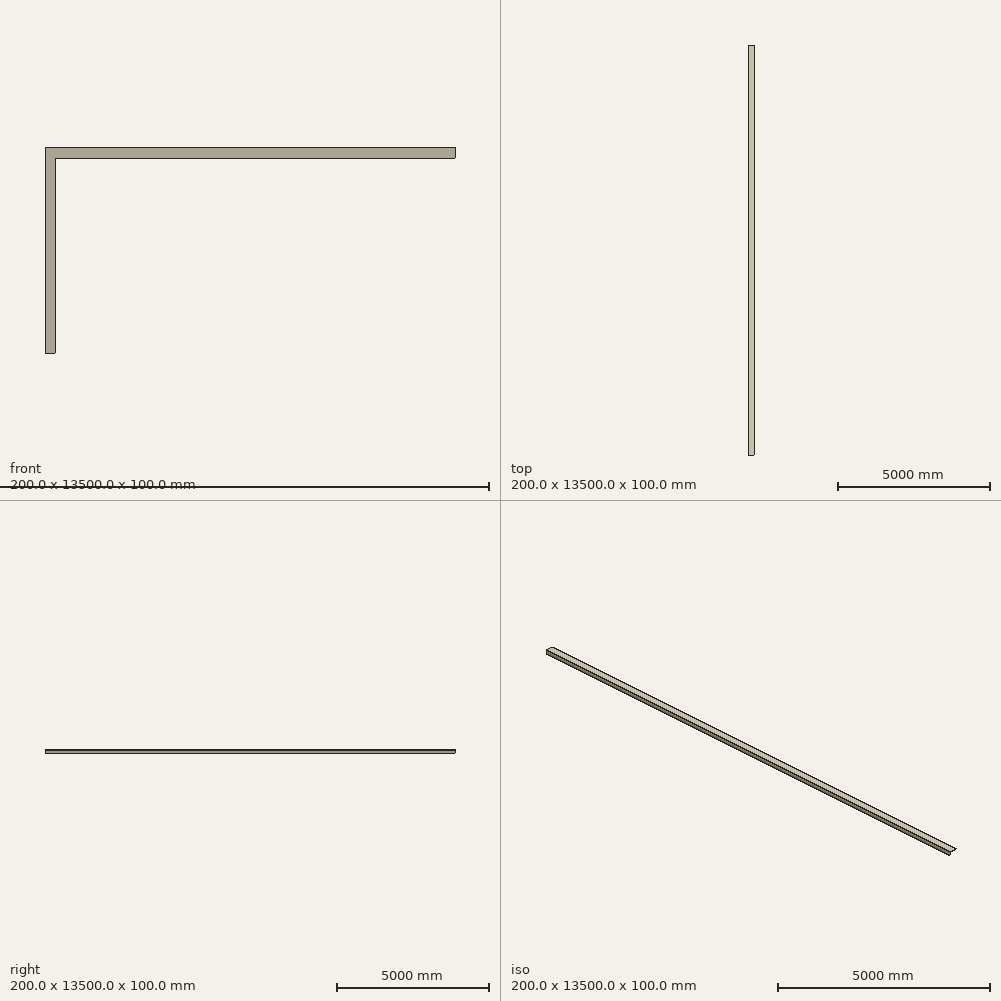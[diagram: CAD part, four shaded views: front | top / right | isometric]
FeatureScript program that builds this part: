
annotation { "Feature Type Name" : "Feature", "Feature Type Description" : "" }
export const myFeature = defineFeature(function(context is Context, id is Id, definition is map)
    precondition{}
    {
        {
            var Q0;
            Q0=qCreatedBy(makeId("Front.planeOp"),FACE);
            var sketch = newSketch(context, id + "F0", { "sketchPlane" : qUnion([Q0])});
            skLineSegment(sketch, "E0", {"start": v(0, 0) * mm, "end": v(0, 100) * mm});
            skLineSegment(sketch, "E1", {"start": v(0, 100) * mm, "end": v(200, 100) * mm});
            skLineSegment(sketch, "E2", {"start": v(200, 100) * mm, "end": v(200, 95) * mm});
            skLineSegment(sketch, "E3", {"start": v(200, 95) * mm, "end": v(5, 95) * mm});
            skLineSegment(sketch, "E4", {"start": v(5, 95) * mm, "end": v(5, 0) * mm});
            skLineSegment(sketch, "E5", {"start": v(5, 0) * mm, "end": v(0, 0) * mm});
            skSolve(sketch);
        }
        {
            var Q0;
            Q0 = qSketchRegion(id + "F0", true);
            extrude(context, id + "F1", {"entities" : qUnion([Q0]), "depth" : 13500 * mm, "offsetDistance" : 25 * mm});
        }
    });
